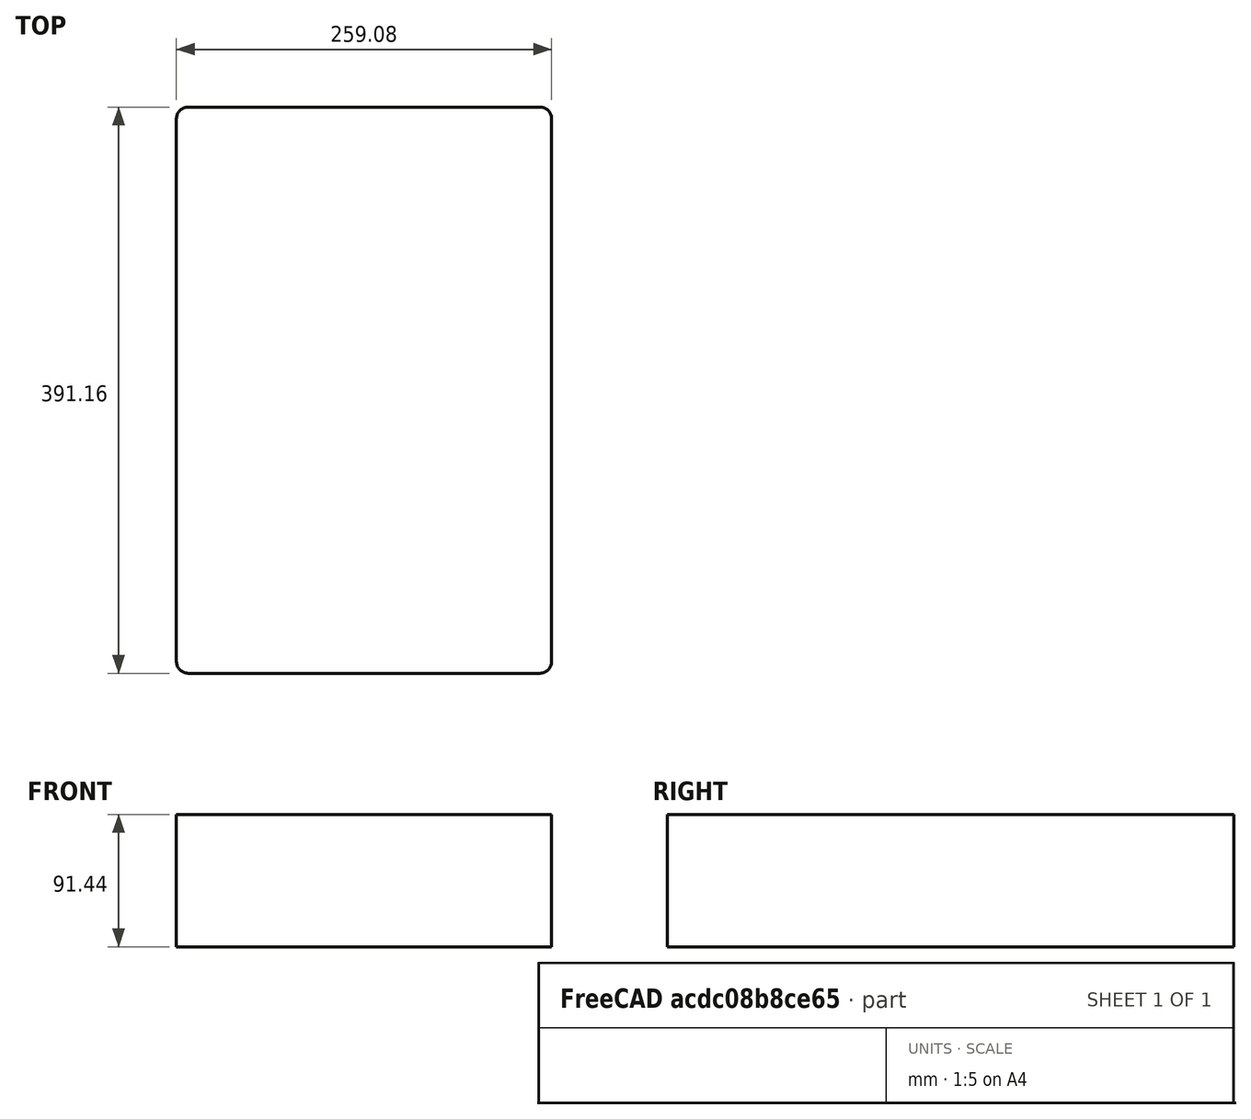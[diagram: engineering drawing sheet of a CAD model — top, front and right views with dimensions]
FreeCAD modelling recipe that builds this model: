
FCSTD DOCUMENT  (FreeCAD 0.20R29177 +426 (Git))
Label: PlayStation5
License: All rights reserved
LicenseURL: http://en.wikipedia.org/wiki/All_rights_reserved
objects: App::DocumentObjectGroup×3, PartDesign::CoordinateSystem×1, App::FeaturePython×1, Sketcher::SketchObject×1, PartDesign::Pad×1, PartDesign::Body×1, App::Part×1
note: 5 computed .brp shape members not serialized (recipe doc carries the construction recipe); baked Part::Feature solids carry a one-line shape summary decoded from their .brp

FEATURE [App::DocumentObjectGroup] Parts
FEATURE [PartDesign::CoordinateSystem] LCS_Origin
  AttacherType = Attacher::AttachEngine3D
  MapMode = 2
  Support = -> [X_Axis]
FEATURE [App::FeaturePython] Variables  # WARN: FeaturePython — macro-defined, semantics opaque (R4)
  Type = App::PropertyContainer
FEATURE [App::DocumentObjectGroup] Constraints
FEATURE [App::DocumentObjectGroup] Configurations
FEATURE [Sketcher::SketchObject] Sketch
  FullyConstrained = true
  MapMode = 5
  Support = -> [XY_Plane001]
  sketch-geometry (10):
    g0: ArcOfCircle CenterX=-121.54 CenterY=187.58 CenterZ=0 NormalX=0 NormalY=0 NormalZ=1 AngleXU=0 Radius=8 StartAngle=1.5708 EndAngle=3.14159
    g1: LineSegment StartX=-121.54 StartY=195.58 StartZ=0 EndX=121.54 EndY=195.58 EndZ=0
    g2: ArcOfCircle CenterX=121.54 CenterY=187.58 CenterZ=0 NormalX=0 NormalY=0 NormalZ=1 AngleXU=0 Radius=8 StartAngle=-9e-16 EndAngle=1.5708
    g3: LineSegment StartX=129.54 StartY=187.58 StartZ=0 EndX=129.54 EndY=-187.58 EndZ=0
    g4: ArcOfCircle CenterX=121.54 CenterY=-187.58 CenterZ=0 NormalX=0 NormalY=0 NormalZ=1 AngleXU=0 Radius=8 StartAngle=4.71239 EndAngle=6.28319
    g5: LineSegment StartX=121.54 StartY=-195.58 StartZ=0 EndX=-121.54 EndY=-195.58 EndZ=0
    g6: ArcOfCircle CenterX=-121.54 CenterY=-187.58 CenterZ=0 NormalX=0 NormalY=0 NormalZ=1 AngleXU=0 Radius=8 StartAngle=3.14159 EndAngle=4.71239
    g7: LineSegment StartX=-129.54 StartY=-187.58 StartZ=0 EndX=-129.54 EndY=187.58 EndZ=0
    g8: GeomPoint X=-129.54 Y=195.58 Z=0
    g9: GeomPoint X=129.54 Y=-195.58 Z=0
  constraints (23):
    c: Tangent(g0,g1) = 1.5708
    c: Tangent(g1,g2) = 1.5708
    c: Tangent(g2,g3) = 1.5708
    c: Tangent(g3,g4) = 1.5708
    c: Tangent(g4,g5) = 1.5708
    c: Tangent(g5,g6) = 1.5708
    c: Tangent(g6,g7) = 1.5708
    c: Tangent(g7,g0) = 1.5708
    c: Horizontal(g1)
    c: Horizontal(g5)
    c: Vertical(g3)
    c: Vertical(g7)
    c: Equal(g0,g2)
    c: Equal(g2,g4)
    c: Equal(g4,g6)
    c: PointOnObject(g8,g1)
    c: PointOnObject(g8,g7)
    c: PointOnObject(g9,g3)
    c: PointOnObject(g9,g5)
    c: Symmetric(g4,g0,g-1)
    c: Radius(g2) = 8
    c: DistanceX(g6,g3) = 259.08
    c: DistanceY(g4,g1) = 391.16
FEATURE [PartDesign::Pad] Pad
  Direction = (0,0,1)
  Length = 91.44
  Length2 = 10
  Profile = -> Sketch
  ReferenceAxis = -> Sketch [N_Axis]
  Type = 0
FEATURE [PartDesign::Body] Body
  Group = -> [Sketch,Pad]
  Origin = -> Origin001
  Tip = -> Pad
FEATURE [App::Part] Assembly
  AssemblyType = Part::Link
  Group = -> [LCS_Origin,Variables,Constraints,Configurations,Body]
  Origin = -> Origin
  Type = Assembly
